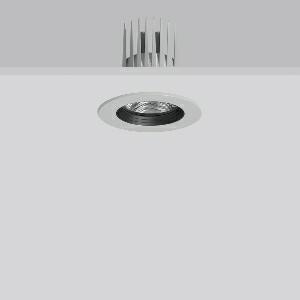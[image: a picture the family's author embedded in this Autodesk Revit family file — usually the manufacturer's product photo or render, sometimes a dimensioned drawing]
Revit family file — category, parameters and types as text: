
# Revit family: heledon_mini_e_901748_004_2_76_aae0
name_source: partatom
category: Lighting Fixtures
units: mm (PartAtom-declared; Revit-internal decimal feet)

## family parameters
Cut with Voids When Loaded = No
Host = Face
Light Source = No
Part Type = Normal
Room Calculation Point = No
Round Connector Dimension = Use Diameter
Shared = No

## types (1)
- HELEDON mini E (1 x LED Modul 927, 3400 lm, 2700)
    Apparent Load = 29 VA
    Approval mark = CE
    CIE Flux Codes = 100 100 100 100 100
    Color Rendering = 92
    Color Temperature = 2700
    Default Elevation = 1800 mm
    Description = Series: HELEDON mini
Round recessed downlight. Housing: die-cast aluminium, powder-coated. Black plastic ring and recessed LED to prevent glare from the side. Optical assembly with reflector made of MIRO-Silver with 98% total light reflection for outstanding efficiency - can be changed without tools. Best colour rendering index Ra>90. Suitable for Recessed ceiling mounting. Installation without tools thanks to spring fastening system. Including separate LED converter with connecting cable 600 mm.High quality converter without flickering and stroboscopic effect. Through-wiring box (5 pole) available as accessory. The following accessories can be mounted without use of tools: interchangeable lenses, decorative glasses, honeycomb louvre, clear and frosted diffusers, white interchangeable plastic ring. 
Colour: silver
Diameter: 124 mm
Height: 3 mm
Cut-out diameter: 114 mm
Recess height: 170 mm
Luminaire: recess height: 120 mm
Lamp: LED
Socket: without socket
Colour temperature: 2700K
Colour rendering index (CRI): 92
System power: 29 W
Rated luminous flux: 3400 lm
Luminous efficiency: 117 lm/W
Control gear: Converter, dimmable, DALI
Protection class: II
Type of protection: IP 20
    Height = 0 mm  [stored 0 ft]
    Lamp = 1 x LED Modul 927
    Lamp Light Flux = 3400 lm
    Lamp count = 1
    Length = 124 mm  [stored 0.406824 ft]
    Lifetime = 50000 h
    Luminous efficacy = 117 lm/W
    Manufacturer = RZB
    ModVariant = No
    Model = 901748.004.2.76
    Mounting Place = Ceiling
    Mounting Type = Recessed
    Number of Poles = 1
    OnlyDefault = Yes
    Power Factor = 1
    Product Name = HELEDON mini E
    Product group = Recessed downlights
    ProductGroupID = 402
    Protection Class = Protection class II
    Protection Degree = IP 20
    RLX_Detail_Level = 1
    RLX_Emergency_Light_Flux = 0 lm
    RLX_Emergency_Type = 0
    RLX_Emergency_Type_DB = No
    RlxData = <blob elided: 127701 chars, md5=62b40f92>
    Socket = socket
    Standby Power = 0 W
    System Light Flux = 3400 lm
    System Power = 29 W
    Type Comments = Product without accessories
    Type Image = 901657.004.jpg
    URL = http://relux.com
    VarID = ---
    Voltage = 230 V
    Voltage Range = 220-240 V
    Weight = 0.00 kg
    Width = 0 mm  [stored 0 ft]

note: [stored X ft] marks values corroborated as IEEE doubles in the binary element streams (Revit-internal decimal feet)

## geometry (parser evidence)
native form markers: Blend x4, Sweep x13
no freeform markers — native parametric forms only
